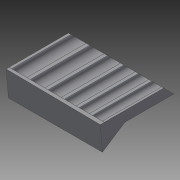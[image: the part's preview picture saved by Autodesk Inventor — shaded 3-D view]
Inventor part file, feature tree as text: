
AUTODESK INVENTOR PART (.ipt)
format: ipt  version: 2015 (Build 190159000, 159)  size: 237,056 bytes
history: native  units: mm
features: sketch x7, projected_geometry x3, plane x2, loft x2
ambient origin geometry x8: Origin, YZ Plane, XZ Plane, XY Plane, X Axis, Y Axis, Z Axis, Center Point
bodies: Body1 (feature_tree)
feature tree (14):
  sketch  "Sketch1"  dims[d0=29.0mm d1=27.5mm]
  sketch  "Sketch4"  dims[d2=25.0mm d3=22.25mm]
  plane  "Work Plane4"
  loft  "Loft1"
  sketch  "Sketch7"  dims[d6=38.25mm]
  loft  "Loft3"
  plane  "Work Plane3"
  sketch  "Sketch5"  dims[d4=20.0mm]
  sketch  "Sketch6"  dims[d5=19.0mm]
  projected_geometry  "Projected Loop2"
  sketch  "Sketch10"  dims[d7=36.25mm]
  projected_geometry  "Projected Loop4"
  sketch  "Sketch11"  dims[d8=33.625mm d9=31.125mm d10=29.5mm d11=0.0mm d12=0.0mm d13=0.0mm d14=0.0mm d15=0.0mm d20=20.0mm d22=20.0mm d23=20.0mm d24=7.0mm d25=4.586mm d51=45.0deg d53=0.0mm d55=29.903294mm d56=29.0mm d57=27.5mm d58=25.0mm d59=22.25mm d60=20.0mm d61=19.0mm d62=30.5mm d63=28.5mm d64=25.875mm d65=23.375mm d66=21.75mm d67=0.0mm d68=0.0mm d69=0.0mm d70=0.0mm d71=0.0mm d72=20.0mm d73=11.75mm d74=16.75mm d75=7.0mm d76=4.586mm d77=29.0mm d78=27.5mm d79=25.0mm d80=22.25mm d81=20.0mm d82=19.0mm d83=30.5mm d84=28.5mm d85=25.875mm d86=23.375mm d87=21.75mm d88=0.0mm d89=0.0mm d90=0.0mm d91=0.0mm d92=0.0mm d93=20.0mm d94=11.75mm d95=16.75mm d96=7.0mm d97=4.586mm d98=100.0mm d99=0.0mm d100=90.0deg d101=0.0mm d102=90.0deg d106=5.0mm d111=14.835299mm d113=25.0mm d114=40.0mm d115=25.0mm d116=40.0mm d117=0.0mm d118=90.0deg d119=0.0mm d120=90.0deg]
  projected_geometry  "Projected Loop5"
